# Revit family: SD 6060 CIR
name_source: partatom
category: Lighting Fixtures
revit_build: Autodesk Revit 2017 (Build: 20160225_1515(x64)
units: mm (PartAtom-declared; Revit-internal decimal feet)

## family parameters
Cut with Voids When Loaded = No
Host = Face
Light Source = Yes
Part Type = Normal
Room Calculation Point = No
Round Connector Dimension = Use Diameter
Shared = No

## types (4) — shared parameters
Color Filter = 16777215
Default Elevation = 1219 mm
Dimming Lamp Color Temperature Shift = <None>
Emit Shape Visible in Rendering = Yes
Emit from Rectangle Length = 570 mm  [stored 1.87008 ft]
Emit from Rectangle Width = 570 mm  [stored 1.87008 ft]
Light Source Symbol Size = 610 mm
Manufacturer = ARLIGHT
Type Image = SD 6060 CIR.JPG

## per-type parameters (varying)
| type | Wattage Comments |
| SDCIR.6060.36.30 | 36 |
| SDCIR.6060.36.40 | 36 |
| SDCIR.6060.28.30 | 28 |
| SDCIR.6060.28.40 | 28 |

note: [stored X ft] marks values corroborated as IEEE doubles in the binary element streams (Revit-internal decimal feet)

## geometry (parser evidence)
native form markers: Sweep x3
no freeform markers — native parametric forms only
